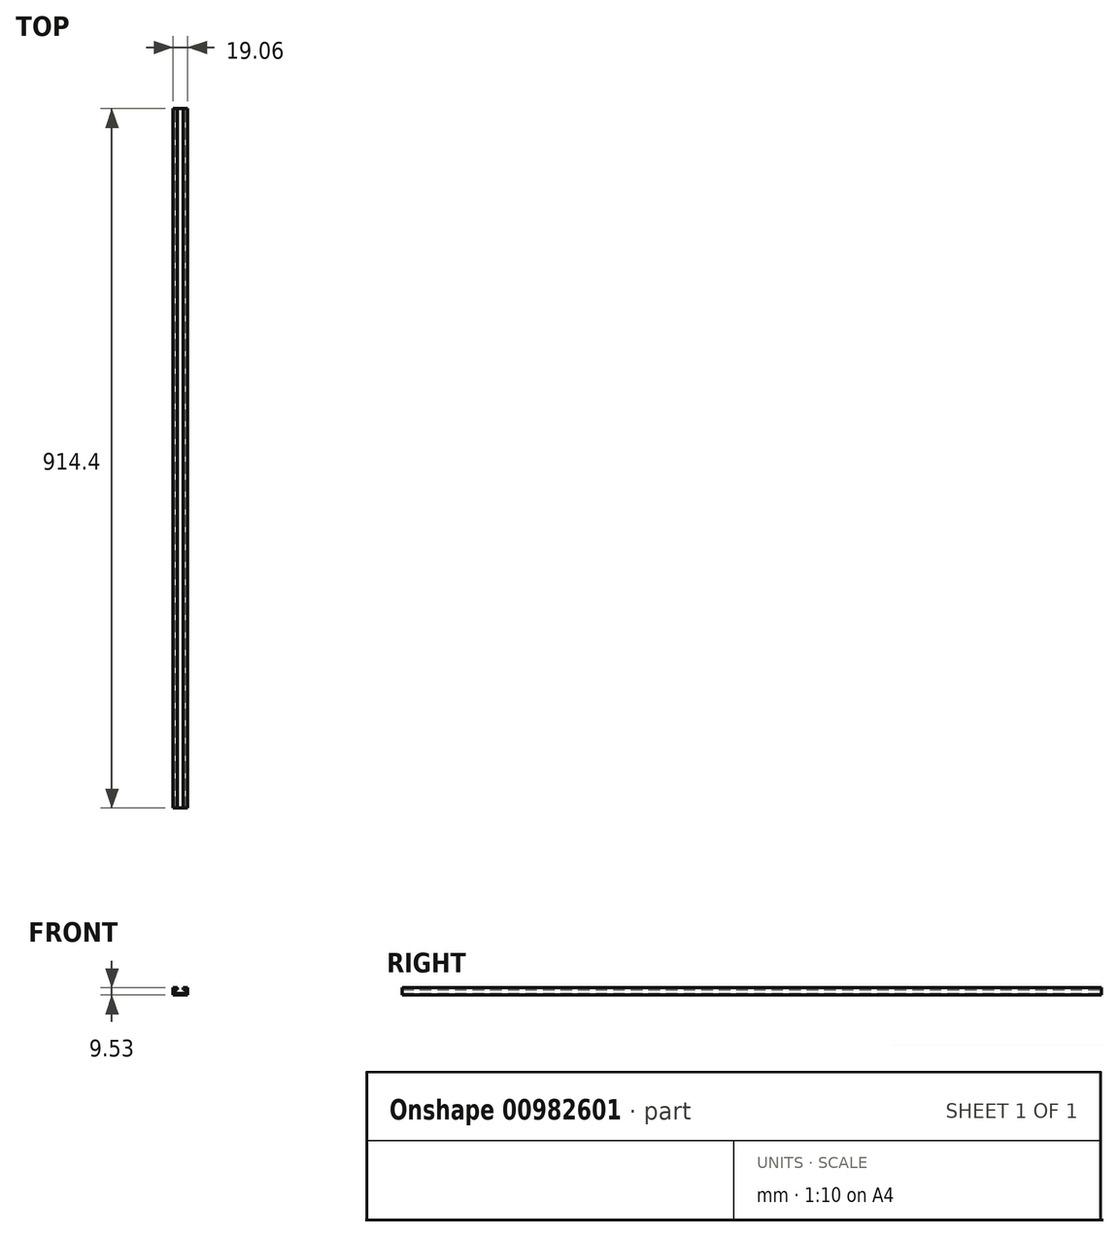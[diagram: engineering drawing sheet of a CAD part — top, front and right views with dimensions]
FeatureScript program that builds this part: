
annotation { "Feature Type Name" : "Feature", "Feature Type Description" : "" }
export const myFeature = defineFeature(function(context is Context, id is Id, definition is map)
    precondition{}
    {
        {
            var Q0;
            Q0=qCreatedBy(makeId("Front.planeOp"),FACE);
            var sketch = newSketch(context, id + "F0", { "sketchPlane" : qUnion([Q0])});
            skLineSegment(sketch, "E0.bottom", {"start": v(-9.53, 0) * mm, "end": v(9.53, 0) * mm});
            skLineSegment(sketch, "E0.top", {"start": v(-9.53, 9.53) * mm, "end": v(-3.81, 9.53) * mm});
            skLineSegment(sketch, "E0.left", {"start": v(-9.53, 0) * mm, "end": v(-9.53, 9.53) * mm});
            skLineSegment(sketch, "E0.right", {"start": v(9.53, 0) * mm, "end": v(9.52, 9.53) * mm});
            skLineSegment(sketch, "E1.bottom", {"start": v(-7.5, 2.03) * mm, "end": v(7.5, 2.03) * mm});
            skLineSegment(sketch, "E1.top", {"start": v(-7.5, 7.5) * mm, "end": v(-3.81, 7.5) * mm});
            skLineSegment(sketch, "E1.left", {"start": v(-7.5, 2.03) * mm, "end": v(-7.5, 7.5) * mm});
            skLineSegment(sketch, "E1.right", {"start": v(7.5, 2.03) * mm, "end": v(7.5, 7.5) * mm});
            skLineSegment(sketch, "E2", {"start": v(-3.81, 9.53) * mm, "end": v(-3.81, 7.5) * mm});
            skLineSegment(sketch, "E3", {"start": v(3.8, 7.5) * mm, "end": v(3.8, 9.53) * mm});
            skLineSegment(sketch, "E4.trimOffspring", {"start": v(3.8, 9.53) * mm, "end": v(9.52, 9.53) * mm});
            skLineSegment(sketch, "E5.trimOffspring", {"start": v(3.8, 7.5) * mm, "end": v(7.5, 7.5) * mm});
            skSolve(sketch);
        }
        {
            var Q0;
            Q0=qSketchRegion(id+"F0",true);
            extrude(context, id + "F1", {"entities" : qUnion([Q0]), "endBound" : BoundingType.SYMMETRIC, "depth" : 914.4 * mm, "hasSecondDirection" : true, "secondDirectionOppositeDirection" : true, "secondDirectionDepth" : 25.4 * mm});
        }
    });
